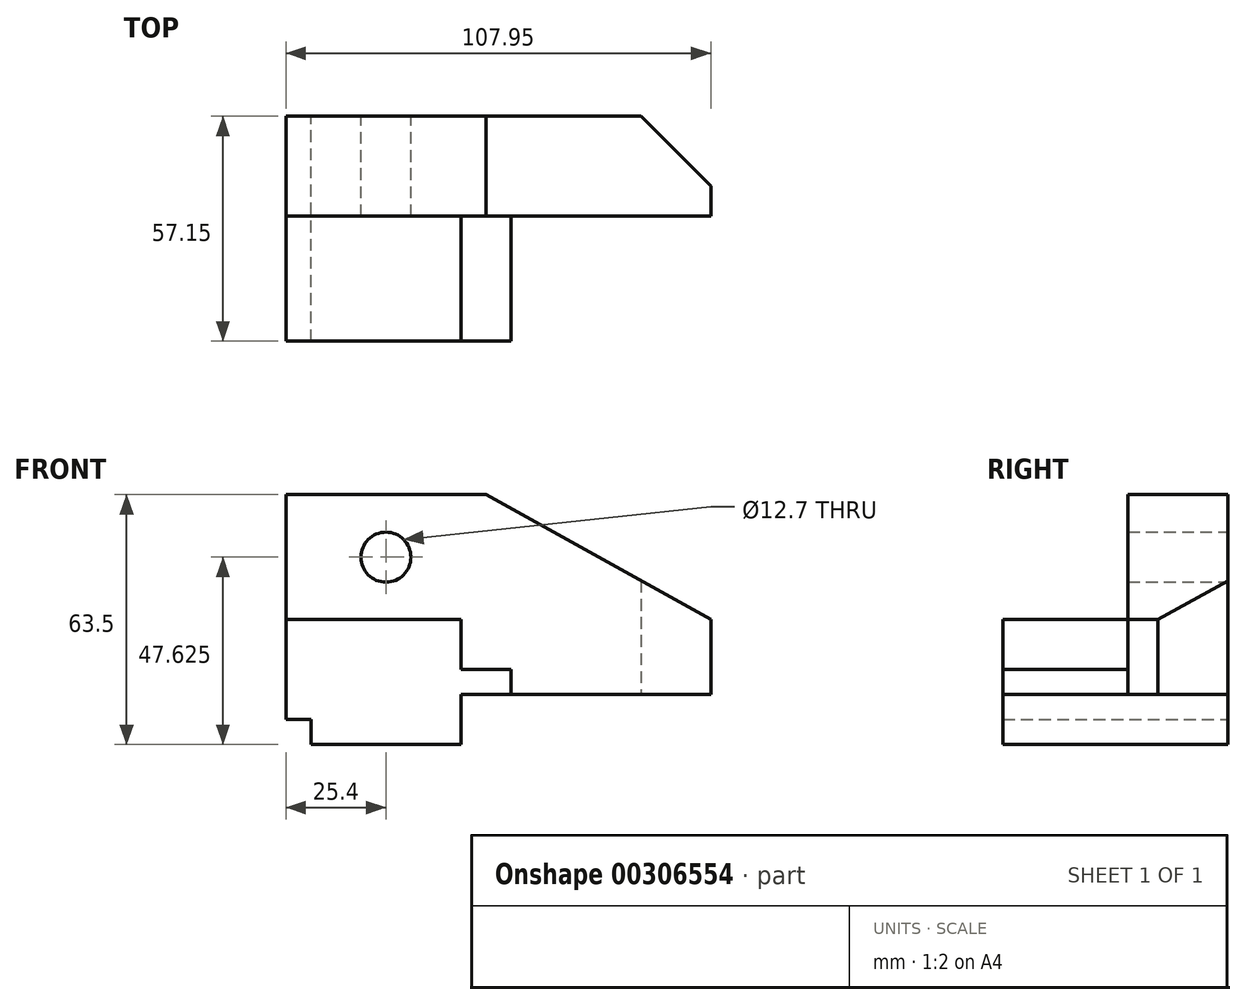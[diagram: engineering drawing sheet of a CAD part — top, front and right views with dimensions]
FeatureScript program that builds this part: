
annotation { "Feature Type Name" : "Feature", "Feature Type Description" : "" }
export const myFeature = defineFeature(function(context is Context, id is Id, definition is map)
    precondition{}
    {
        {
            var Q0;
            Q0=qCreatedBy(makeId("Front.planeOp"),FACE);
            var sketch = newSketch(context, id + "F0", { "sketchPlane" : qUnion([Q0])});
            skLineSegment(sketch, "E0", {"start": v(0, 0) * mm, "end": v(0, 6.35) * mm});
            skLineSegment(sketch, "E1", {"start": v(0, 6.35) * mm, "end": v(-6.35, 6.35) * mm});
            skLineSegment(sketch, "E2", {"start": v(-6.35, 6.35) * mm, "end": v(-6.35, 31.75) * mm});
            skLineSegment(sketch, "E3", {"start": v(-6.35, 31.75) * mm, "end": v(38.1, 31.75) * mm});
            skLineSegment(sketch, "E4", {"start": v(38.1, 31.75) * mm, "end": v(38.1, 19.05) * mm});
            skLineSegment(sketch, "E5", {"start": v(38.1, 19.05) * mm, "end": v(50.8, 19.05) * mm});
            skLineSegment(sketch, "E6", {"start": v(50.8, 19.05) * mm, "end": v(50.8, 12.7) * mm});
            skLineSegment(sketch, "E7", {"start": v(50.8, 12.7) * mm, "end": v(38.1, 12.7) * mm});
            skLineSegment(sketch, "E8", {"start": v(38.1, 12.7) * mm, "end": v(38.1, 0) * mm});
            skLineSegment(sketch, "E9", {"start": v(38.1, 0) * mm, "end": v(0, 0) * mm});
            skLineSegment(sketch, "E10", {"start": v(-6.35, 31.75) * mm, "end": v(-6.35, 63.5) * mm});
            skLineSegment(sketch, "E11", {"start": v(-6.35, 63.5) * mm, "end": v(44.45, 63.5) * mm});
            skLineSegment(sketch, "E12", {"start": v(44.45, 63.5) * mm, "end": v(101.6, 31.75) * mm});
            skLineSegment(sketch, "E13", {"start": v(101.6, 12.7) * mm, "end": v(50.8, 12.7) * mm});
            skLineSegment(sketch, "E14", {"start": v(101.6, 31.75) * mm, "end": v(101.6, 12.7) * mm});
            skCircle(sketch, "E15", {"center": v(19.05, 47.62) * mm, "radius": 6.35 * mm});
            skPoint(sketch, "E15.centerSnap0", {"position": v(-6.35, 47.63) * mm});
            skSolve(sketch);
        }
        {
            var Q0;
            Q0=makeQuery(id+"F0.imprint","IMPRINT",FACE,{"disambiguationData":[TD([[makeQuery(id+"F0.imprint","IMPRINT",EDGE,{"derivedFrom":sQuery(id+"F0.wireOp",EDGE,"E3")}),1.0]])]});
            extrude(context, id + "F1", {"entities" : qUnion([Q0]), "depth" : 25.4 * mm});
        }
        {
            var Q0;
            Q0=makeQuery(id+"F0.imprint","IMPRINT",FACE,{"disambiguationData":[TD([[makeQuery(id+"F0.imprint","IMPRINT",EDGE,{"derivedFrom":sQuery(id+"F0.wireOp",EDGE,"E0")}),-1.0]])]});
            extrude(context, id + "F2", {"entities" : qUnion([Q0]), "operationType" : NewBodyOperationType.ADD, "depth" : 57.15 * mm});
        }
        {
            var Q0;
            Q0=makeQuery(id+"F2.boolean.opBoolean","MERGE",FACE,{"derivedFrom":[makeQuery(id+"F1.opExtrude","SWEPT_FACE",FACE,{"disambiguationData":[OSD([sQuery(id+"F0.wireOp",EDGE,"E13")])]}),makeQuery(id+"F2.opExtrude","SWEPT_FACE",FACE,{"disambiguationData":[OSD([sQuery(id+"F0.wireOp",EDGE,"E7")])]})]});
            var sketch = newSketch(context, id + "F3", { "sketchPlane" : qUnion([Q0])});
            skLineSegment(sketch, "E16", {"start": v(101.6, 25.4) * mm, "end": v(101.6, 17.78) * mm});
            skLineSegment(sketch, "E17", {"start": v(101.6, 17.78) * mm, "end": v(83.82, 0) * mm});
            skLineSegment(sketch, "E18", {"start": v(83.82, 0) * mm, "end": v(101.6, 0) * mm});
            skLineSegment(sketch, "E19", {"start": v(101.6, 0) * mm, "end": v(101.6, 17.78) * mm});
            skSolve(sketch);
        }
        {
            var Q0;
            Q0=makeQuery(id+"F3.imprint","IMPRINT",FACE,{"disambiguationData":[TD([[makeQuery(id+"F3.imprint","IMPRINT",EDGE,{"derivedFrom":sQuery(id+"F3.wireOp",EDGE,"E17")}),1.0]])]});
            extrude(context, id + "F4", {"entities" : qUnion([Q0]), "operationType" : NewBodyOperationType.REMOVE, "endBound" : BoundingType.THROUGH_ALL, "oppositeDirection" : true, "depth" : 25.4 * mm});
        }
    });
